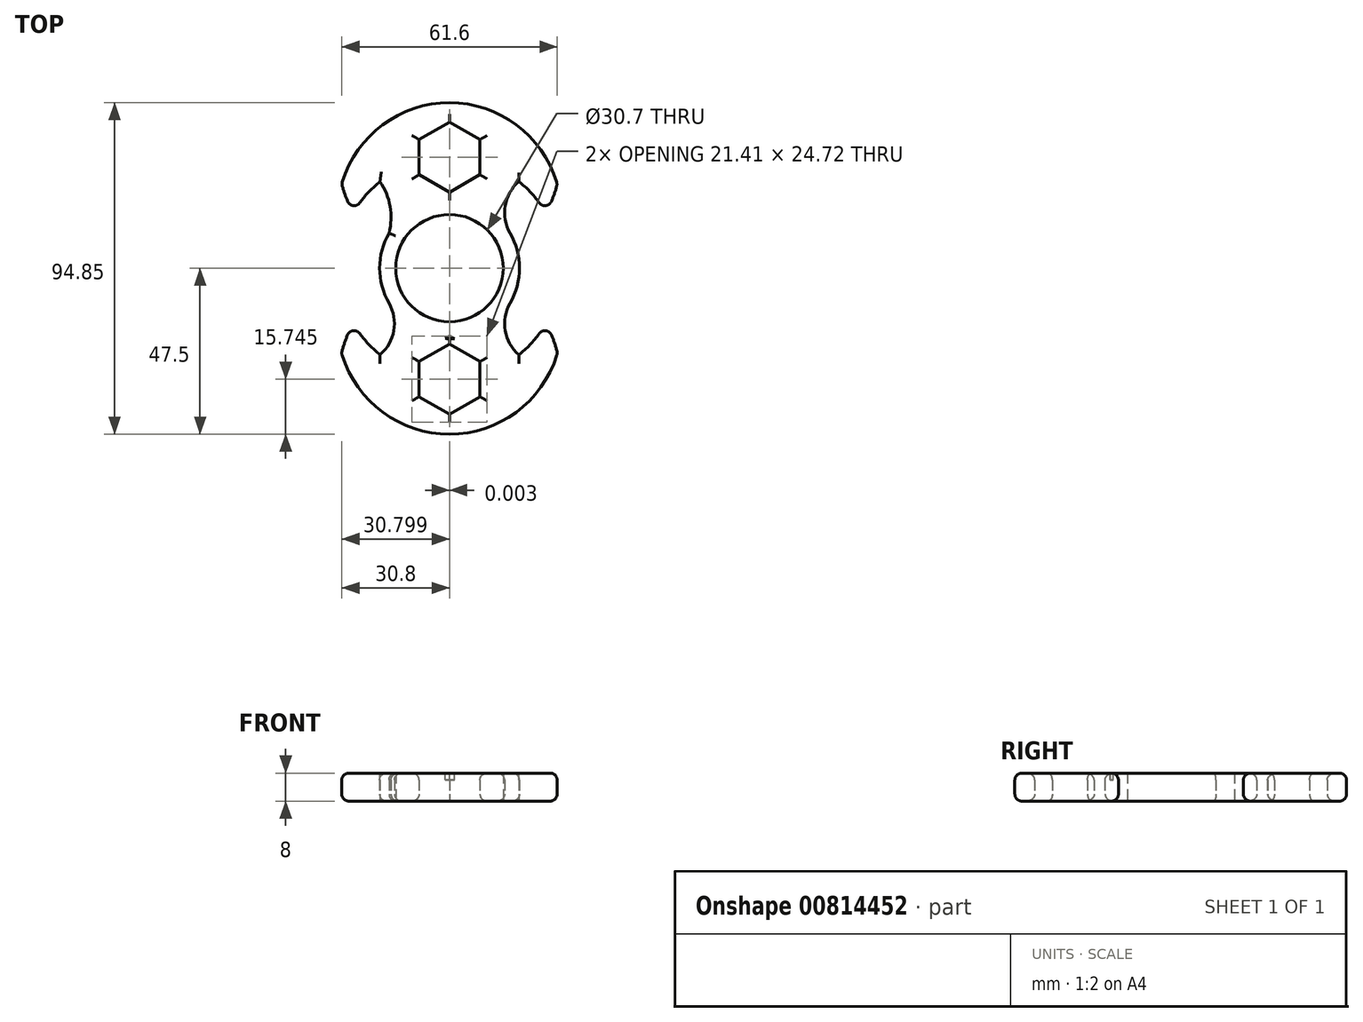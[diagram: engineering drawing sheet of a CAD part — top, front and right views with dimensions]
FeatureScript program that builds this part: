
annotation { "Feature Type Name" : "Feature", "Feature Type Description" : "" }
export const myFeature = defineFeature(function(context is Context, id is Id, definition is map)
    precondition{}
    {
        {
            var Q0;
            Q0=qCreatedBy(makeId("Top.planeOp"),FACE);
            var sketch = newSketch(context, id + "F0", { "sketchPlane" : qUnion([Q0])});
            skCircle(sketch, "E0", {"center": v(0, 0) * mm, "radius": 15.35 * mm});
            skArc(sketch, "E1", {"start": v(17.3, -10.04) * mm, "mid": v(20, 0) * mm, "end": v(17.3, 10.04) * mm});
            skCircle(sketch, "E2", {"center": v(0, 31.75) * mm, "radius": 10.05 * mm});
            skPoint(sketch, "E3.orphan", {"position": v(0, -30.51) * mm});
            skCircle(sketch, "E4", {"center": v(0, -31.75) * mm, "radius": 10.05 * mm});
            skArc(sketch, "E5", {"start": v(30.87, -24.32) * mm, "mid": v(29.49, -19.98) * mm, "end": v(27.5, -15.88) * mm});
            skArc(sketch, "E6", {"start": v(27.5, 15.88) * mm, "mid": v(29.43, 19.84) * mm, "end": v(30.8, 24.03) * mm});
            skArc(sketch, "E7", {"start": v(-27.5, -15.88) * mm, "mid": v(-24.09, -20.7) * mm, "end": v(-19.84, -24.8) * mm});
            skArc(sketch, "E8", {"start": v(30.8, 24.03) * mm, "mid": v(0, 47.35) * mm, "end": v(-30.8, 24.03) * mm});
            skArc(sketch, "E9", {"start": v(-30.87, -24.31) * mm, "mid": v(0, -47.5) * mm, "end": v(30.87, -24.32) * mm});
            skArc(sketch, "E10.trimOffspring", {"start": v(-27.5, -15.88) * mm, "mid": v(-29.49, -19.97) * mm, "end": v(-30.87, -24.31) * mm});
            skArc(sketch, "E11.trimOffspring", {"start": v(19.84, -24.8) * mm, "mid": v(24.09, -20.7) * mm, "end": v(27.5, -15.88) * mm});
            skArc(sketch, "E12.trimOffspring", {"start": v(-30.8, 24.03) * mm, "mid": v(-29.43, 19.84) * mm, "end": v(-27.5, 15.88) * mm});
            skArc(sketch, "E13.trimOffspring", {"start": v(27.5, 15.88) * mm, "mid": v(24.09, 20.7) * mm, "end": v(19.84, 24.8) * mm});
            skArc(sketch, "E14", {"start": v(19.84, 24.8) * mm, "mid": v(15.92, 17.88) * mm, "end": v(17.3, 10.04) * mm});
            skArc(sketch, "E15", {"start": v(17.3, -10.04) * mm, "mid": v(15.92, -17.88) * mm, "end": v(19.84, -24.8) * mm});
            skArc(sketch, "E16", {"start": v(-19.84, -24.8) * mm, "mid": v(-15.92, -17.88) * mm, "end": v(-17.3, -10.04) * mm});
            skArc(sketch, "E17.trimOffspring", {"start": v(-17.3, 10.04) * mm, "mid": v(-16.99, 17.68) * mm, "end": v(-19.88, 24.76) * mm});
            skArc(sketch, "E18.trimOffspring", {"start": v(-19.88, 24.76) * mm, "mid": v(-24.1, 20.68) * mm, "end": v(-27.5, 15.88) * mm});
            skArc(sketch, "E19.trimOffspring", {"start": v(-17.3, 10.04) * mm, "mid": v(-20, 0) * mm, "end": v(-17.3, -10.04) * mm});
            skCircle(sketch, "E20.cCircle", {"center": v(0, 31.75) * mm, "radius": 10.05 * mm, "construction": true});
            skLineSegment(sketch, "E20.0", {"start": v(0, 21.7) * mm, "end": v(-8.7, 26.73) * mm});
            skLineSegment(sketch, "E20.1", {"start": v(-8.7, 26.73) * mm, "end": v(-8.7, 36.78) * mm});
            skLineSegment(sketch, "E20.2", {"start": v(-8.7, 36.78) * mm, "end": v(0, 41.8) * mm});
            skLineSegment(sketch, "E20.3", {"start": v(0, 41.8) * mm, "end": v(8.7, 36.78) * mm});
            skLineSegment(sketch, "E20.4", {"start": v(8.7, 36.78) * mm, "end": v(8.7, 26.73) * mm});
            skLineSegment(sketch, "E20.5", {"start": v(8.7, 26.73) * mm, "end": v(0, 21.7) * mm});
            skCircle(sketch, "E21.cCircle", {"center": v(0, -31.75) * mm, "radius": 10.05 * mm, "construction": true});
            skLineSegment(sketch, "E21.0", {"start": v(0, -21.7) * mm, "end": v(8.7, -26.73) * mm});
            skLineSegment(sketch, "E21.1", {"start": v(8.7, -26.73) * mm, "end": v(8.7, -36.78) * mm});
            skLineSegment(sketch, "E21.2", {"start": v(8.7, -36.78) * mm, "end": v(0, -41.8) * mm});
            skLineSegment(sketch, "E21.3", {"start": v(0, -41.8) * mm, "end": v(-8.7, -36.78) * mm});
            skLineSegment(sketch, "E21.4", {"start": v(-8.7, -36.78) * mm, "end": v(-8.7, -26.73) * mm});
            skLineSegment(sketch, "E21.5", {"start": v(-8.7, -26.73) * mm, "end": v(0, -21.7) * mm});
            skCircle(sketch, "E22", {"center": v(0, 0) * mm, "radius": 31.75 * mm, "construction": true});
            skLineSegment(sketch, "E23.bottom", {"start": v(-17.3, 10.04) * mm, "end": v(17.3, 10.04) * mm, "construction": true});
            skLineSegment(sketch, "E23.top", {"start": v(-17.3, -10.04) * mm, "end": v(17.3, -10.04) * mm, "construction": true});
            skLineSegment(sketch, "E23.left", {"start": v(-17.3, 10.04) * mm, "end": v(-17.3, -10.04) * mm, "construction": true});
            skLineSegment(sketch, "E23.right", {"start": v(17.3, 10.04) * mm, "end": v(17.3, -10.04) * mm, "construction": true});
            skLineSegment(sketch, "E24.bottom", {"start": v(19.84, -24.8) * mm, "end": v(-19.84, -24.8) * mm, "construction": true});
            skLineSegment(sketch, "E24.top", {"start": v(19.84, 24.8) * mm, "end": v(-19.84, 24.8) * mm, "construction": true});
            skLineSegment(sketch, "E24.left", {"start": v(19.84, -24.8) * mm, "end": v(19.84, 24.8) * mm, "construction": true});
            skLineSegment(sketch, "E24.right", {"start": v(-19.84, -24.8) * mm, "end": v(-19.84, 24.8) * mm, "construction": true});
            skLineSegment(sketch, "E25.bottom", {"start": v(-7.5, 18.5) * mm, "end": v(7.5, 18.5) * mm, "construction": true});
            skLineSegment(sketch, "E25.left", {"start": v(-7.5, 18.5) * mm, "end": v(-7.5, -18.5) * mm, "construction": true});
            skLineSegment(sketch, "E25.right", {"start": v(7.5, 18.5) * mm, "end": v(7.5, -18.5) * mm, "construction": true});
            skPoint(sketch, "E26", {"position": v(0, 18.5) * mm});
            skSolve(sketch);
        }
        {
            var Q0;
            {var subQ0=sQuery(id+"F0.wireOp",EDGE,"E20.0");Q0=makeQuery(id+"F0.imprint","IMPRINT",FACE,{"disambiguationData":[TD([[makeQuery(id+"F0.imprint","IMPRINT",EDGE,{"derivedFrom":subQ0}),1.0]])]});}
            var Q1;
            {var subQ0=sQuery(id+"F0.wireOp",EDGE,"E20.5");Q1=makeQuery(id+"F0.imprint","IMPRINT",FACE,{"disambiguationData":[TD([[makeQuery(id+"F0.imprint","IMPRINT",EDGE,{"derivedFrom":subQ0}),1.0]])]});}
            var Q2;
            {var subQ0=sQuery(id+"F0.wireOp",EDGE,"E20.4");Q2=makeQuery(id+"F0.imprint","IMPRINT",FACE,{"disambiguationData":[TD([[makeQuery(id+"F0.imprint","IMPRINT",EDGE,{"derivedFrom":subQ0}),1.0]])]});}
            var Q3;
            {var subQ0=sQuery(id+"F0.wireOp",EDGE,"E20.2");Q3=makeQuery(id+"F0.imprint","IMPRINT",FACE,{"disambiguationData":[TD([[makeQuery(id+"F0.imprint","IMPRINT",EDGE,{"derivedFrom":subQ0}),1.0]])]});}
            var Q4;
            {var subQ0=sQuery(id+"F0.wireOp",EDGE,"E20.3");Q4=makeQuery(id+"F0.imprint","IMPRINT",FACE,{"disambiguationData":[TD([[makeQuery(id+"F0.imprint","IMPRINT",EDGE,{"derivedFrom":subQ0}),1.0]])]});}
            var Q5;
            {var subQ0=sQuery(id+"F0.wireOp",EDGE,"E20.1");Q5=makeQuery(id+"F0.imprint","IMPRINT",FACE,{"disambiguationData":[TD([[makeQuery(id+"F0.imprint","IMPRINT",EDGE,{"derivedFrom":subQ0}),1.0]])]});}
            var Q6;
            {var subQ0=sQuery(id+"F0.wireOp",EDGE,"E21.0");Q6=makeQuery(id+"F0.imprint","IMPRINT",FACE,{"disambiguationData":[TD([[makeQuery(id+"F0.imprint","IMPRINT",EDGE,{"derivedFrom":subQ0}),1.0]])]});}
            var Q7;
            {var subQ0=sQuery(id+"F0.wireOp",EDGE,"E21.1");Q7=makeQuery(id+"F0.imprint","IMPRINT",FACE,{"disambiguationData":[TD([[makeQuery(id+"F0.imprint","IMPRINT",EDGE,{"derivedFrom":subQ0}),1.0]])]});}
            var Q8;
            {var subQ0=sQuery(id+"F0.wireOp",EDGE,"E21.2");Q8=makeQuery(id+"F0.imprint","IMPRINT",FACE,{"disambiguationData":[TD([[makeQuery(id+"F0.imprint","IMPRINT",EDGE,{"derivedFrom":subQ0}),1.0]])]});}
            var Q9;
            Q9=makeQuery(id+"F0.imprint","IMPRINT",FACE,{"disambiguationData":[TD([[makeQuery(id+"F0.imprint","IMPRINT",EDGE,{"derivedFrom":sQuery(id+"F0.wireOp",EDGE,"E0")}),-1.0]])]});
            var Q10;
            {var subQ0=sQuery(id+"F0.wireOp",EDGE,"E21.3");Q10=makeQuery(id+"F0.imprint","IMPRINT",FACE,{"disambiguationData":[TD([[makeQuery(id+"F0.imprint","IMPRINT",EDGE,{"derivedFrom":subQ0}),1.0]])]});}
            var Q11;
            {var subQ0=sQuery(id+"F0.wireOp",EDGE,"E21.4");Q11=makeQuery(id+"F0.imprint","IMPRINT",FACE,{"disambiguationData":[TD([[makeQuery(id+"F0.imprint","IMPRINT",EDGE,{"derivedFrom":subQ0}),1.0]])]});}
            var Q12;
            {var subQ0=sQuery(id+"F0.wireOp",EDGE,"E21.5");Q12=makeQuery(id+"F0.imprint","IMPRINT",FACE,{"disambiguationData":[TD([[makeQuery(id+"F0.imprint","IMPRINT",EDGE,{"derivedFrom":subQ0}),1.0]])]});}
            var Q13;
            Q13=makeQuery(id+"F0.imprint","IMPRINT",FACE,{"disambiguationData":[TD([[makeQuery(id+"F0.imprint","IMPRINT",EDGE,{"derivedFrom":sQuery(id+"F0.wireOp",EDGE,"b09e6dd1-dab8-4b64-9b37-ad7a02245aec.sketch_text.stroke-16")}),1.0]])]});
            var Q14;
            Q14=makeQuery(id+"F0.imprint","IMPRINT",FACE,{"disambiguationData":[TD([[makeQuery(id+"F0.imprint","IMPRINT",EDGE,{"derivedFrom":sQuery(id+"F0.wireOp",EDGE,"b09e6dd1-dab8-4b64-9b37-ad7a02245aec.sketch_text.stroke-0")}),-1.0]])]});
            var Q15;
            Q15=makeQuery(id+"F0.imprint","IMPRINT",FACE,{"disambiguationData":[TD([[makeQuery(id+"F0.imprint","IMPRINT",EDGE,{"derivedFrom":sQuery(id+"F0.wireOp",EDGE,"b3a1ebe3-2c7f-47d1-8247-27ddfe72ac5a.sketch_text.stroke-23")}),1.0]])]});
            var Q16;
            Q16=makeQuery(id+"F0.imprint","IMPRINT",FACE,{"disambiguationData":[TD([[makeQuery(id+"F0.imprint","IMPRINT",EDGE,{"derivedFrom":sQuery(id+"F0.wireOp",EDGE,"b3a1ebe3-2c7f-47d1-8247-27ddfe72ac5a.sketch_text.stroke-16")}),1.0]])]});
            var Q17;
            Q17=makeQuery(id+"F0.imprint","IMPRINT",FACE,{"disambiguationData":[TD([[makeQuery(id+"F0.imprint","IMPRINT",EDGE,{"derivedFrom":sQuery(id+"F0.wireOp",EDGE,"b3a1ebe3-2c7f-47d1-8247-27ddfe72ac5a.sketch_text.stroke-0")}),-1.0]])]});
            extrude(context, id + "F1", {"entities" : qUnion([Q0, Q1, Q2, Q3, Q4, Q5, Q6, Q7, Q8, Q9, Q10, Q11, Q12, Q13, Q14, Q15, Q16, Q17]), "depth" : 8 * mm, "offsetDistance" : 25 * mm});
        }
        {
            var Q0;
            Q0=makeQuery(id+"F1.opExtrude","CAP_EDGE",EDGE,{"disambiguationData":[OSD([sQuery(id+"F0.wireOp",EDGE,"E8")])],"isStart":false});
            var Q1;
            Q1=makeQuery(id+"F1.opExtrude","CAP_EDGE",EDGE,{"disambiguationData":[OSD([sQuery(id+"F0.wireOp",EDGE,"E12.trimOffspring")])],"isStart":false});
            var Q2;
            Q2=makeQuery(id+"F1.opExtrude","CAP_EDGE",EDGE,{"disambiguationData":[OSD([sQuery(id+"F0.wireOp",EDGE,"E18.trimOffspring")])],"isStart":false});
            var Q3;
            Q3=makeQuery(id+"F1.opExtrude","CAP_EDGE",EDGE,{"disambiguationData":[OSD([sQuery(id+"F0.wireOp",EDGE,"E17.trimOffspring")])],"isStart":false});
            var Q4;
            Q4=makeQuery(id+"F1.opExtrude","CAP_EDGE",EDGE,{"disambiguationData":[OSD([sQuery(id+"F0.wireOp",EDGE,"E15")])],"isStart":false});
            var Q5;
            Q5=makeQuery(id+"F1.opExtrude","CAP_EDGE",EDGE,{"disambiguationData":[OSD([sQuery(id+"F0.wireOp",EDGE,"E13.trimOffspring")])],"isStart":false});
            var Q6;
            Q6=makeQuery(id+"F1.opExtrude","CAP_EDGE",EDGE,{"disambiguationData":[OSD([sQuery(id+"F0.wireOp",EDGE,"E6")])],"isStart":false});
            var Q7;
            Q7=makeQuery(id+"F1.opExtrude","CAP_EDGE",EDGE,{"disambiguationData":[OSD([sQuery(id+"F0.wireOp",EDGE,"E9")])],"isStart":false});
            var Q8;
            Q8=makeQuery(id+"F1.opExtrude","CAP_EDGE",EDGE,{"disambiguationData":[OSD([sQuery(id+"F0.wireOp",EDGE,"E5")])],"isStart":false});
            var Q9;
            Q9=makeQuery(id+"F1.opExtrude","CAP_EDGE",EDGE,{"disambiguationData":[OSD([sQuery(id+"F0.wireOp",EDGE,"E7")])],"isStart":false});
            var Q10;
            Q10=makeQuery(id+"F1.opExtrude","CAP_EDGE",EDGE,{"disambiguationData":[OSD([sQuery(id+"F0.wireOp",EDGE,"E10.trimOffspring")])],"isStart":false});
            var Q11;
            Q11=makeQuery(id+"F1.opExtrude","CAP_EDGE",EDGE,{"disambiguationData":[OSD([sQuery(id+"F0.wireOp",EDGE,"E11.trimOffspring")])],"isStart":false});
            var Q12;
            Q12=makeQuery(id+"F1.opExtrude","CAP_EDGE",EDGE,{"disambiguationData":[OSD([sQuery(id+"F0.wireOp",EDGE,"E9")])],"isStart":true});
            var Q13;
            Q13=makeQuery(id+"F1.opExtrude","CAP_EDGE",EDGE,{"disambiguationData":[OSD([sQuery(id+"F0.wireOp",EDGE,"E5")])],"isStart":true});
            var Q14;
            Q14=makeQuery(id+"F1.opExtrude","CAP_EDGE",EDGE,{"disambiguationData":[OSD([sQuery(id+"F0.wireOp",EDGE,"E11.trimOffspring")])],"isStart":true});
            var Q15;
            Q15=makeQuery(id+"F1.opExtrude","CAP_EDGE",EDGE,{"disambiguationData":[OSD([sQuery(id+"F0.wireOp",EDGE,"E15")])],"isStart":true});
            var Q16;
            Q16=makeQuery(id+"F1.opExtrude","CAP_EDGE",EDGE,{"disambiguationData":[OSD([sQuery(id+"F0.wireOp",EDGE,"E13.trimOffspring")])],"isStart":true});
            var Q17;
            Q17=makeQuery(id+"F1.opExtrude","CAP_EDGE",EDGE,{"disambiguationData":[OSD([sQuery(id+"F0.wireOp",EDGE,"E8")])],"isStart":true});
            var Q18;
            Q18=makeQuery(id+"F1.opExtrude","CAP_EDGE",EDGE,{"disambiguationData":[OSD([sQuery(id+"F0.wireOp",EDGE,"E12.trimOffspring")])],"isStart":true});
            var Q19;
            Q19=makeQuery(id+"F1.opExtrude","CAP_EDGE",EDGE,{"disambiguationData":[OSD([sQuery(id+"F0.wireOp",EDGE,"E17.trimOffspring")])],"isStart":true});
            var Q20;
            Q20=makeQuery(id+"F1.opExtrude","CAP_EDGE",EDGE,{"disambiguationData":[OSD([sQuery(id+"F0.wireOp",EDGE,"E10.trimOffspring")])],"isStart":true});
            var Q21;
            Q21=makeQuery(id+"F1.opExtrude","CAP_EDGE",EDGE,{"disambiguationData":[OSD([sQuery(id+"F0.wireOp",EDGE,"E7")])],"isStart":true});
            var Q22;
            Q22=makeQuery(id+"F1.opExtrude","CAP_EDGE",EDGE,{"disambiguationData":[OSD([sQuery(id+"F0.wireOp",EDGE,"E18.trimOffspring")])],"isStart":true});
            var Q23;
            Q23=makeQuery(id+"F1.opExtrude","SWEPT_EDGE",EDGE,{"disambiguationData":[OSD([sQuery(id+"F0.wireOp",EDGE,"E12.trimOffspring"),sQuery(id+"F0.wireOp",EDGE,"E18.trimOffspring")])]});
            var Q24;
            Q24=makeQuery(id+"F1.opExtrude","SWEPT_EDGE",EDGE,{"disambiguationData":[OSD([sQuery(id+"F0.wireOp",EDGE,"E6"),sQuery(id+"F0.wireOp",EDGE,"E13.trimOffspring")])]});
            var Q25;
            Q25=makeQuery(id+"F1.opExtrude","CAP_EDGE",EDGE,{"disambiguationData":[OSD([sQuery(id+"F0.wireOp",EDGE,"E6")])],"isStart":true});
            var Q26;
            Q26=makeQuery(id+"F1.opExtrude","SWEPT_EDGE",EDGE,{"disambiguationData":[OSD([sQuery(id+"F0.wireOp",EDGE,"E5"),sQuery(id+"F0.wireOp",EDGE,"E9")])]});
            var Q27;
            Q27=makeQuery(id+"F1.opExtrude","SWEPT_EDGE",EDGE,{"disambiguationData":[OSD([sQuery(id+"F0.wireOp",EDGE,"E5"),sQuery(id+"F0.wireOp",EDGE,"E11.trimOffspring")])]});
            var Q28;
            Q28=makeQuery(id+"F1.opExtrude","SWEPT_EDGE",EDGE,{"disambiguationData":[OSD([sQuery(id+"F0.wireOp",EDGE,"E6"),sQuery(id+"F0.wireOp",EDGE,"E8")])]});
            var Q29;
            Q29=makeQuery(id+"F1.opExtrude","SWEPT_EDGE",EDGE,{"disambiguationData":[OSD([sQuery(id+"F0.wireOp",EDGE,"E8"),sQuery(id+"F0.wireOp",EDGE,"E12.trimOffspring")])]});
            var Q30;
            Q30=makeQuery(id+"F1.opExtrude","SWEPT_EDGE",EDGE,{"disambiguationData":[OSD([sQuery(id+"F0.wireOp",EDGE,"E7"),sQuery(id+"F0.wireOp",EDGE,"E10.trimOffspring")])]});
            var Q31;
            Q31=makeQuery(id+"F1.opExtrude","SWEPT_EDGE",EDGE,{"disambiguationData":[OSD([sQuery(id+"F0.wireOp",EDGE,"E9"),sQuery(id+"F0.wireOp",EDGE,"E10.trimOffspring")])]});
            var Q32;
            Q32=makeQuery(id+"F1.opExtrude","CAP_EDGE",EDGE,{"disambiguationData":[OSD([sQuery(id+"F0.wireOp",EDGE,"E20.1")])],"isStart":false});
            var Q33;
            Q33=makeQuery(id+"F1.opExtrude","CAP_EDGE",EDGE,{"disambiguationData":[OSD([sQuery(id+"F0.wireOp",EDGE,"E20.2")])],"isStart":false});
            var Q34;
            Q34=makeQuery(id+"F1.opExtrude","CAP_EDGE",EDGE,{"disambiguationData":[OSD([sQuery(id+"F0.wireOp",EDGE,"E20.3")])],"isStart":false});
            var Q35;
            Q35=makeQuery(id+"F1.opExtrude","CAP_EDGE",EDGE,{"disambiguationData":[OSD([sQuery(id+"F0.wireOp",EDGE,"E20.4")])],"isStart":false});
            var Q36;
            Q36=makeQuery(id+"F1.opExtrude","CAP_EDGE",EDGE,{"disambiguationData":[OSD([sQuery(id+"F0.wireOp",EDGE,"E20.5")])],"isStart":false});
            var Q37;
            Q37=makeQuery(id+"F1.opExtrude","CAP_EDGE",EDGE,{"disambiguationData":[OSD([sQuery(id+"F0.wireOp",EDGE,"E21.5")])],"isStart":false});
            var Q38;
            Q38=makeQuery(id+"F1.opExtrude","CAP_EDGE",EDGE,{"disambiguationData":[OSD([sQuery(id+"F0.wireOp",EDGE,"E21.0")])],"isStart":false});
            var Q39;
            Q39=makeQuery(id+"F1.opExtrude","CAP_EDGE",EDGE,{"disambiguationData":[OSD([sQuery(id+"F0.wireOp",EDGE,"E21.4")])],"isStart":false});
            var Q40;
            Q40=makeQuery(id+"F1.opExtrude","CAP_EDGE",EDGE,{"disambiguationData":[OSD([sQuery(id+"F0.wireOp",EDGE,"E21.3")])],"isStart":false});
            var Q41;
            Q41=makeQuery(id+"F1.opExtrude","CAP_EDGE",EDGE,{"disambiguationData":[OSD([sQuery(id+"F0.wireOp",EDGE,"E21.2")])],"isStart":false});
            var Q42;
            Q42=makeQuery(id+"F1.opExtrude","CAP_EDGE",EDGE,{"disambiguationData":[OSD([sQuery(id+"F0.wireOp",EDGE,"E21.1")])],"isStart":false});
            var Q43;
            Q43=makeQuery(id+"F1.opExtrude","CAP_EDGE",EDGE,{"disambiguationData":[OSD([sQuery(id+"F0.wireOp",EDGE,"E21.4")])],"isStart":true});
            var Q44;
            Q44=makeQuery(id+"F1.opExtrude","CAP_EDGE",EDGE,{"disambiguationData":[OSD([sQuery(id+"F0.wireOp",EDGE,"E21.3")])],"isStart":true});
            var Q45;
            Q45=makeQuery(id+"F1.opExtrude","CAP_EDGE",EDGE,{"disambiguationData":[OSD([sQuery(id+"F0.wireOp",EDGE,"E21.2")])],"isStart":true});
            var Q46;
            Q46=makeQuery(id+"F1.opExtrude","CAP_EDGE",EDGE,{"disambiguationData":[OSD([sQuery(id+"F0.wireOp",EDGE,"E21.1")])],"isStart":true});
            var Q47;
            Q47=makeQuery(id+"F1.opExtrude","CAP_EDGE",EDGE,{"disambiguationData":[OSD([sQuery(id+"F0.wireOp",EDGE,"E21.0")])],"isStart":true});
            var Q48;
            Q48=makeQuery(id+"F1.opExtrude","CAP_EDGE",EDGE,{"disambiguationData":[OSD([sQuery(id+"F0.wireOp",EDGE,"E21.5")])],"isStart":true});
            var Q49;
            Q49=makeQuery(id+"F1.opExtrude","CAP_EDGE",EDGE,{"disambiguationData":[OSD([sQuery(id+"F0.wireOp",EDGE,"E20.5")])],"isStart":true});
            var Q50;
            Q50=makeQuery(id+"F1.opExtrude","CAP_EDGE",EDGE,{"disambiguationData":[OSD([sQuery(id+"F0.wireOp",EDGE,"E20.2")])],"isStart":true});
            var Q51;
            Q51=makeQuery(id+"F1.opExtrude","CAP_EDGE",EDGE,{"disambiguationData":[OSD([sQuery(id+"F0.wireOp",EDGE,"E20.3")])],"isStart":true});
            var Q52;
            Q52=makeQuery(id+"F1.opExtrude","CAP_EDGE",EDGE,{"disambiguationData":[OSD([sQuery(id+"F0.wireOp",EDGE,"E20.0")])],"isStart":true});
            var Q53;
            Q53=makeQuery(id+"F1.opExtrude","CAP_EDGE",EDGE,{"disambiguationData":[OSD([sQuery(id+"F0.wireOp",EDGE,"E20.4")])],"isStart":true});
            var Q54;
            Q54=makeQuery(id+"F1.opExtrude","CAP_EDGE",EDGE,{"disambiguationData":[OSD([sQuery(id+"F0.wireOp",EDGE,"E20.1")])],"isStart":true});
            var Q55;
            Q55=makeQuery(id+"F1.opExtrude","CAP_EDGE",EDGE,{"disambiguationData":[OSD([sQuery(id+"F0.wireOp",EDGE,"E20.0")])],"isStart":false});
            var Q56;
            Q56=makeQuery(id+"F1.opExtrude","CAP_EDGE",EDGE,{"disambiguationData":[OSD([sQuery(id+"F0.wireOp",EDGE,"E16")])],"isStart":false});
            var Q57;
            Q57=makeQuery(id+"F1.opExtrude","CAP_EDGE",EDGE,{"disambiguationData":[OSD([sQuery(id+"F0.wireOp",EDGE,"E14")])],"isStart":true});
            var Q58;
            Q58=makeQuery(id+"F1.opExtrude","CAP_EDGE",EDGE,{"disambiguationData":[OSD([sQuery(id+"F0.wireOp",EDGE,"E16")])],"isStart":true});
            var Q59;
            Q59=makeQuery(id+"F1.opExtrude","CAP_EDGE",EDGE,{"disambiguationData":[OSD([sQuery(id+"F0.wireOp",EDGE,"E14")])],"isStart":false});
            var Q60;
            Q60=makeQuery(id+"F1.opExtrude","CAP_EDGE",EDGE,{"disambiguationData":[OSD([sQuery(id+"F0.wireOp",EDGE,"E1")])],"isStart":false});
            var Q61;
            Q61=makeQuery(id+"F1.opExtrude","CAP_EDGE",EDGE,{"disambiguationData":[OSD([sQuery(id+"F0.wireOp",EDGE,"E1")])],"isStart":true});
            var Q62;
            Q62=makeQuery(id+"F1.opExtrude","CAP_EDGE",EDGE,{"disambiguationData":[OSD([sQuery(id+"F0.wireOp",EDGE,"E19.trimOffspring")])],"isStart":true});
            var Q63;
            Q63=makeQuery(id+"F1.opExtrude","CAP_EDGE",EDGE,{"disambiguationData":[OSD([sQuery(id+"F0.wireOp",EDGE,"E19.trimOffspring")])],"isStart":false});
            fillet(context, id + "F2", {"entities" : qUnion([Q0, Q1, Q2, Q3, Q4, Q5, Q6, Q7, Q8, Q9, Q10, Q11, Q12, Q13, Q14, Q15, Q16, Q17, Q18, Q19, Q20, Q21, Q22, Q23, Q24, Q25, Q26, Q27, Q28, Q29, Q30, Q31, Q32, Q33, Q34, Q35, Q36, Q37, Q38, Q39, Q40, Q41, Q42, Q43, Q44, Q45, Q46, Q47, Q48, Q49, Q50, Q51, Q52, Q53, Q54, Q55, Q56, Q57, Q58, Q59, Q60, Q61, Q62, Q63]), "radius" : 2 * mm, "tangentPropagation" : true, "allowEdgeOverflow" : false});
        }
        {
            var Q0;
            Q0=makeQuery(id+"F1.opExtrude","CAP_FACE",FACE,{"disambiguationData":[OSD([sQuery(id+"F0.wireOp",EDGE,"E0"),sQuery(id+"F0.wireOp",EDGE,"E1"),sQuery(id+"F0.wireOp",EDGE,"E5"),sQuery(id+"F0.wireOp",EDGE,"E6"),sQuery(id+"F0.wireOp",EDGE,"E7"),sQuery(id+"F0.wireOp",EDGE,"E8"),sQuery(id+"F0.wireOp",EDGE,"E9"),sQuery(id+"F0.wireOp",EDGE,"E10.trimOffspring"),sQuery(id+"F0.wireOp",EDGE,"E11.trimOffspring"),sQuery(id+"F0.wireOp",EDGE,"E12.trimOffspring"),sQuery(id+"F0.wireOp",EDGE,"E13.trimOffspring"),sQuery(id+"F0.wireOp",EDGE,"E14"),sQuery(id+"F0.wireOp",EDGE,"E15"),sQuery(id+"F0.wireOp",EDGE,"E16"),sQuery(id+"F0.wireOp",EDGE,"E17.trimOffspring"),sQuery(id+"F0.wireOp",EDGE,"E18.trimOffspring"),sQuery(id+"F0.wireOp",EDGE,"E19.trimOffspring"),sQuery(id+"F0.wireOp",EDGE,"E20.0"),sQuery(id+"F0.wireOp",EDGE,"E20.1"),sQuery(id+"F0.wireOp",EDGE,"E20.2"),sQuery(id+"F0.wireOp",EDGE,"E20.3"),sQuery(id+"F0.wireOp",EDGE,"E20.4"),sQuery(id+"F0.wireOp",EDGE,"E20.5"),sQuery(id+"F0.wireOp",EDGE,"E21.0"),sQuery(id+"F0.wireOp",EDGE,"E21.1"),sQuery(id+"F0.wireOp",EDGE,"E21.2"),sQuery(id+"F0.wireOp",EDGE,"E21.3"),sQuery(id+"F0.wireOp",EDGE,"E21.4"),sQuery(id+"F0.wireOp",EDGE,"E21.5")])],"isStart":false});
            var sketch = newSketch(context, id + "F3", { "sketchPlane" : qUnion([Q0])});
            skText(sketch, "E27", { "text": "A", "fontName": "RobotoSlab-Bold.ttf"});
            skText(sketch, "E28", { "text": "B", "fontName": "RobotoSlab-Bold.ttf"});
            const initialGuessF3  = {"E27": [-0.00424, 0.01231, 1, 0, 0.008], "E28": [0.00386, -0.0123, -1, 0, 0.008]};
            skSetInitialGuess(sketch, initialGuessF3);
            skSolve(sketch);
        }
        {
            var Q0;
            Q0=makeQuery(id+"F3.imprint","IMPRINT",FACE,{"disambiguationData":[TD([[makeQuery(id+"F3.imprint","IMPRINT",EDGE,{"derivedFrom":sQuery(id+"F3.wireOp",EDGE,"E28.sketch_text.stroke-0")}),-1.0]])]});
            var Q1;
            Q1=makeQuery(id+"F3.imprint","IMPRINT",FACE,{"disambiguationData":[TD([[makeQuery(id+"F3.imprint","IMPRINT",EDGE,{"derivedFrom":sQuery(id+"F3.wireOp",EDGE,"E27.sketch_text.stroke-0")}),-1.0]])]});
            var Q2;
            Q2=qConstructionFilter(qBodyType(qCreatedBy(id+"F3",EDGE),BodyType.WIRE),ConstructionObject.NO);
            extrude(context, id + "F4", {"entities" : qUnion([Q0, Q1]), "operationType" : NewBodyOperationType.REMOVE, "surfaceEntities" : qUnion([Q2]), "oppositeDirection" : true, "depth" : 2 * mm, "offsetDistance" : 25 * mm});
        }
    });
